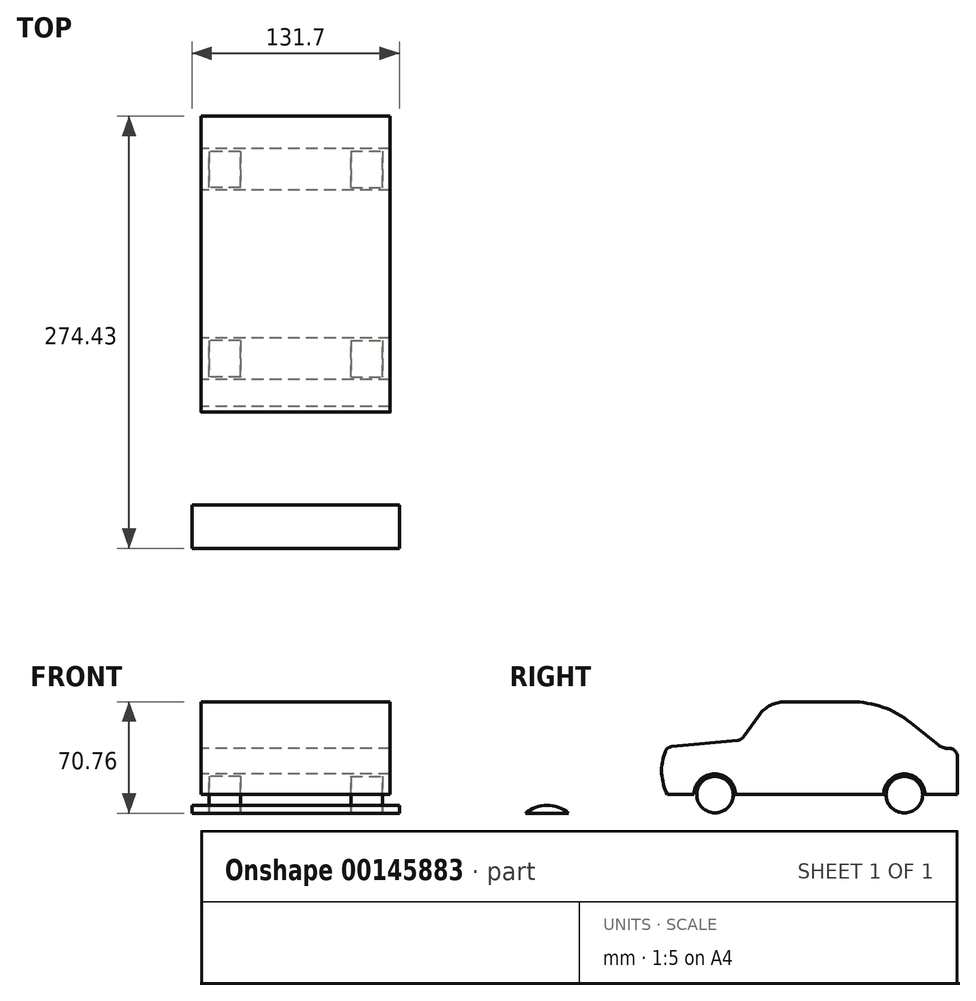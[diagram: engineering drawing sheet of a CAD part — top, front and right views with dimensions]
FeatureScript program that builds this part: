
annotation { "Feature Type Name" : "Feature", "Feature Type Description" : "" }
export const myFeature = defineFeature(function(context is Context, id is Id, definition is map)
    precondition{}
    {
        {
            var Q0;
            Q0=qCreatedBy(makeId("Right.planeOp"),FACE);
            var sketch = newSketch(context, id + "F0", { "sketchPlane" : qUnion([Q0])});
            skArc(sketch, "E0", {"start": v(-32, 0) * mm, "mid": v(-45.15, 13.15) * mm, "end": v(-58.3, 0) * mm});
            skLineSegment(sketch, "E1", {"start": v(-75.25, 30.28) * mm, "end": v(-28.35, 34.65) * mm});
            skLineSegment(sketch, "E2", {"start": v(-28.35, 34.65) * mm, "end": v(-10.86, 58.93) * mm});
            skLineSegment(sketch, "E3", {"start": v(108.97, 0) * mm, "end": v(88.35, 0) * mm});
            skArc(sketch, "E4", {"start": v(-75.25, 30.28) * mm, "mid": v(-78.9, 15.14) * mm, "end": v(-75.25, 0) * mm});
            skLineSegment(sketch, "E5", {"start": v(99.73, 29.28) * mm, "end": v(108.97, 29.28) * mm});
            skLineSegment(sketch, "E6", {"start": v(108.97, 29.28) * mm, "end": v(108.97, 0) * mm});
            skLineSegment(sketch, "E7", {"start": v(99.73, 29.28) * mm, "end": v(62.9, 58.93) * mm});
            skLineSegment(sketch, "E8", {"start": v(62.9, 58.93) * mm, "end": v(-10.86, 58.93) * mm});
            skArc(sketch, "E9", {"start": v(88.35, 0) * mm, "mid": v(75.25, 13.1) * mm, "end": v(62.14, 0) * mm});
            skLineSegment(sketch, "E10", {"start": v(-32, 0) * mm, "end": v(62.14, 0) * mm});
            skLineSegment(sketch, "E11", {"start": v(-75.25, 0) * mm, "end": v(-58.3, 0) * mm});
            skSolve(sketch);
        }
        {
            var Q0;
            Q0=makeQuery(id+"F0.imprint","IMPRINT",FACE,{"disambiguationData":[TD([[makeQuery(id+"F0.imprint","IMPRINT",EDGE,{"derivedFrom":sQuery(id+"F0.wireOp",EDGE,"E0")}),-1.0]])]});
            extrude(context, id + "F1", {"entities" : qUnion([Q0]), "endBound" : BoundingType.SYMMETRIC, "depth" : 120 * mm});
        }
        {
            var Q0;
            Q0=makeQuery(id+"F1.opExtrude","SWEPT_EDGE",EDGE,{"disambiguationData":[OSD([sQuery(id+"F0.wireOp",EDGE,"E1"),sQuery(id+"F0.wireOp",EDGE,"E4")])]});
            var Q1;
            Q1=makeQuery(id+"F1.opExtrude","SWEPT_EDGE",EDGE,{"disambiguationData":[OSD([sQuery(id+"F0.wireOp",EDGE,"E1"),sQuery(id+"F0.wireOp",EDGE,"E2")])]});
            fillet(context, id + "F2", {"entities" : qUnion([Q0, Q1]), "radius" : 5.08 * mm, "tangentPropagation" : true, "allowEdgeOverflow" : false});
        }
        {
            var Q0;
            Q0=makeQuery(id+"F1.opExtrude","SWEPT_EDGE",EDGE,{"disambiguationData":[OSD([sQuery(id+"F0.wireOp",EDGE,"E2"),sQuery(id+"F0.wireOp",EDGE,"E8")])]});
            fillet(context, id + "F3", {"entities" : qUnion([Q0]), "radius" : 20 * mm, "tangentPropagation" : true, "allowEdgeOverflow" : false});
        }
        {
            var Q0;
            Q0=makeQuery(id+"F1.opExtrude","SWEPT_EDGE",EDGE,{"disambiguationData":[OSD([sQuery(id+"F0.wireOp",EDGE,"E7"),sQuery(id+"F0.wireOp",EDGE,"E8")])]});
            fillet(context, id + "F4", {"entities" : qUnion([Q0]), "radius" : 60 * mm, "tangentPropagation" : true, "allowEdgeOverflow" : false});
        }
        {
            var Q0;
            Q0=makeQuery(id+"F1.opExtrude","SWEPT_EDGE",EDGE,{"disambiguationData":[OSD([sQuery(id+"F0.wireOp",EDGE,"E5"),sQuery(id+"F0.wireOp",EDGE,"E7")])]});
            fillet(context, id + "F5", {"entities" : qUnion([Q0]), "radius" : 10 * mm, "tangentPropagation" : true, "allowEdgeOverflow" : false});
        }
        {
            var Q0;
            Q0=makeQuery(id+"F1.opExtrude","SWEPT_EDGE",EDGE,{"disambiguationData":[OSD([sQuery(id+"F0.wireOp",EDGE,"E5"),sQuery(id+"F0.wireOp",EDGE,"E6")])]});
            fillet(context, id + "F6", {"entities" : qUnion([Q0]), "radius" : 5.08 * mm, "tangentPropagation" : true, "allowEdgeOverflow" : false});
        }
        {
            var Q0;
            Q0=qCreatedBy(makeId("Right.planeOp"),FACE);
            cPlane(context, id + "F7", {"entities" : qUnion([Q0]), "cplaneType" : CPlaneType.OFFSET, "offset" : 45 * mm, "width" : 152.4 * mm, "height" : 152.4 * mm});
        }
        {
            var Q0;
            Q0=qCreatedBy(id+"F7.planeOp",FACE);
            var sketch = newSketch(context, id + "F8", { "sketchPlane" : qUnion([Q0])});
            skCircle(sketch, "E12", {"center": v(-44.99, 0) * mm, "radius": 11.59 * mm});
            skCircle(sketch, "E13", {"center": v(75.32, 0) * mm, "radius": 11.6 * mm});
            skSolve(sketch);
        }
        {
            var Q0;
            Q0=makeQuery(id+"F8.imprint","IMPRINT",FACE,{"disambiguationData":[TD([[makeQuery(id+"F8.imprint","IMPRINT",EDGE,{"derivedFrom":sQuery(id+"F8.wireOp",EDGE,"E12")}),1.0]])]});
            var Q1;
            Q1=makeQuery(id+"F8.imprint","IMPRINT",FACE,{"disambiguationData":[TD([[makeQuery(id+"F8.imprint","IMPRINT",EDGE,{"derivedFrom":sQuery(id+"F8.wireOp",EDGE,"E13")}),1.0]])]});
            extrude(context, id + "F9", {"entities" : qUnion([Q0, Q1]), "endBound" : BoundingType.SYMMETRIC, "oppositeDirection" : true, "depth" : 20 * mm});
        }
        {
            var Q0;
            Q0=qCreatedBy(makeId("Right.planeOp"),FACE);
            cPlane(context, id + "F10", {"entities" : qUnion([Q0]), "cplaneType" : CPlaneType.OFFSET, "offset" : 40 * mm, "width" : 152.4 * mm, "height" : 152.4 * mm});
        }
        {
            var Q0;
            Q0=qCreatedBy(makeId("Right.planeOp"),FACE);
            var sketch = newSketch(context, id + "F11", { "sketchPlane" : qUnion([Q0])});
            skLineSegment(sketch, "E14", {"start": v(-45.3, -11.83) * mm, "end": v(-137.92, -11.83) * mm});
            skLineSegment(sketch, "E15", {"start": v(-45.3, -11.83) * mm, "end": v(143.44, -11.83) * mm});
            skLineSegment(sketch, "E16", {"start": v(-137.92, -11.83) * mm, "end": v(-366.58, -11.83) * mm});
            skArc(sketch, "E17", {"start": v(-137.92, -11.83) * mm, "mid": v(-151.69, -6.74) * mm, "end": v(-165.46, -11.83) * mm});
            skSolve(sketch);
        }
        {
            var Q0;
            {var subQ0=sQuery(id+"F11.wireOp",EDGE,"E17");Q0=makeQuery(id+"F11.imprint","IMPRINT",FACE,{"disambiguationData":[TD([[makeQuery(id+"F11.imprint","IMPRINT",EDGE,{"derivedFrom":subQ0}),1.0]])]});}
            extrude(context, id + "F12", {"entities" : qUnion([Q0]), "endBound" : BoundingType.SYMMETRIC, "depth" : 131.7 * mm});
        }
        {
            var Q0;
            Q0=qCreatedBy(id+"F10.planeOp",FACE);
            cPlane(context, id + "F13", {"entities" : qUnion([Q0]), "cplaneType" : CPlaneType.OFFSET, "offset" : 85 * mm, "oppositeDirection" : true, "width" : 152.4 * mm, "height" : 152.4 * mm});
        }
        {
            var Q0;
            Q0=qCreatedBy(id+"F13.planeOp",FACE);
            var sketch = newSketch(context, id + "F14", { "sketchPlane" : qUnion([Q0])});
            skCircle(sketch, "E18", {"center": v(75.1, 0) * mm, "radius": 11.54 * mm});
            skCircle(sketch, "E19", {"center": v(-44.92, 0) * mm, "radius": 11.58 * mm});
            skSolve(sketch);
        }
        {
            var Q0;
            Q0=makeQuery(id+"F14.imprint","IMPRINT",FACE,{"disambiguationData":[TD([[makeQuery(id+"F14.imprint","IMPRINT",EDGE,{"derivedFrom":sQuery(id+"F14.wireOp",EDGE,"E19")}),1.0]])]});
            var Q1;
            Q1=makeQuery(id+"F14.imprint","IMPRINT",FACE,{"disambiguationData":[TD([[makeQuery(id+"F14.imprint","IMPRINT",EDGE,{"derivedFrom":sQuery(id+"F14.wireOp",EDGE,"E18")}),1.0]])]});
            extrude(context, id + "F15", {"entities" : qUnion([Q0, Q1]), "endBound" : BoundingType.SYMMETRIC, "depth" : 20 * mm});
        }
    });
